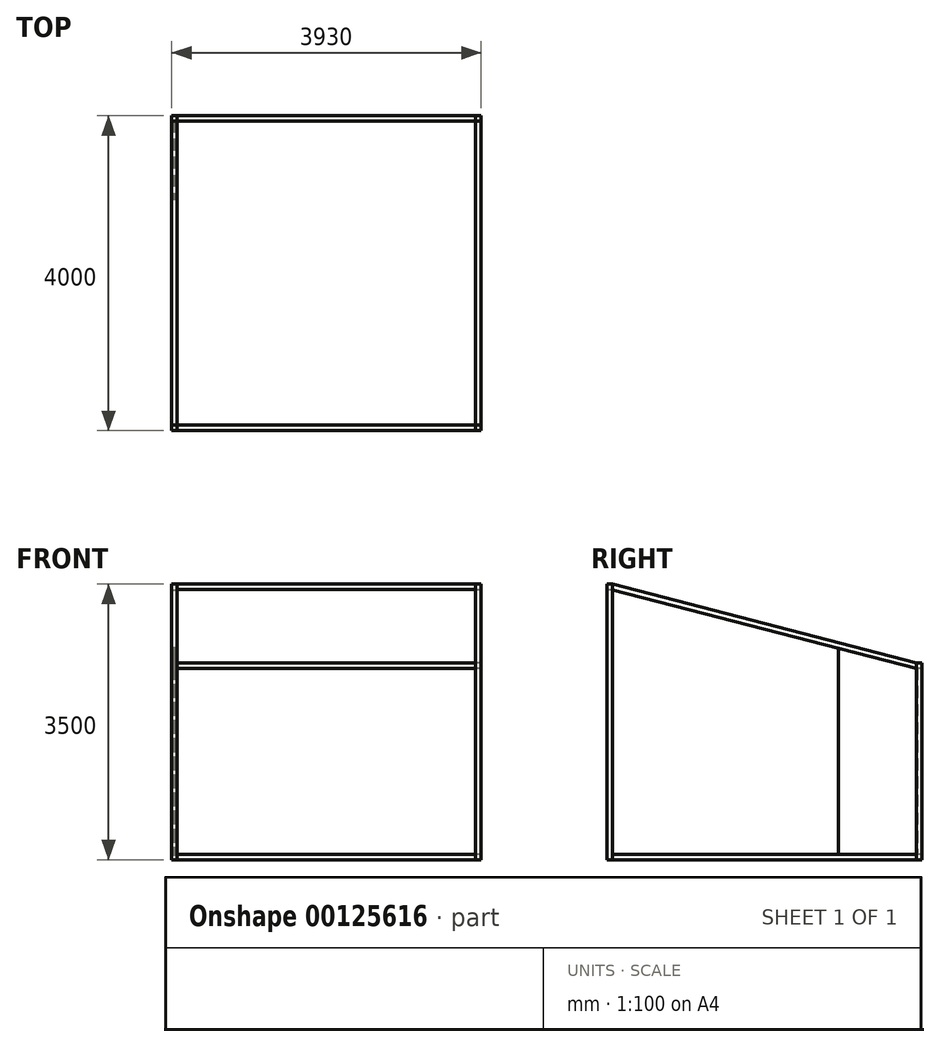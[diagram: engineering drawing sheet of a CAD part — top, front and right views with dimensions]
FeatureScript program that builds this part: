
annotation { "Feature Type Name" : "Feature", "Feature Type Description" : "" }
export const myFeature = defineFeature(function(context is Context, id is Id, definition is map)
    precondition{}
    {
        {
            assignVariable(context, id + "F0", {"name" : "D", "anyValue" : 70});
        }
        {
            var Q0;
            Q0=qCreatedBy(makeId("Front.planeOp"),FACE);
            var sketch = newSketch(context, id + "F1", { "sketchPlane" : qUnion([Q0])});
            skLineSegment(sketch, "E0.bottom", {"start": v(1965, -1750) * mm, "end": v(-1965, -1750) * mm});
            skLineSegment(sketch, "E0.top", {"start": v(1965, 1750) * mm, "end": v(-1965, 1750) * mm});
            skLineSegment(sketch, "E0.left", {"start": v(1965, -1750) * mm, "end": v(1965, 1750) * mm});
            skLineSegment(sketch, "E0.right", {"start": v(-1965, -1750) * mm, "end": v(-1965, 1750) * mm});
            skPoint(sketch, "E0.middle", {"position": v(0, 0) * mm});
            skSolve(sketch);
        }
        {
            var Q0;
            Q0=qCreatedBy(makeId("Front.planeOp"),FACE);
            var sketch = newSketch(context, id + "F2", { "sketchPlane" : qUnion([Q0])});
            skLineSegment(sketch, "E1.bottom", {"start": v(-1965, 1750) * mm, "end": v(-1895, 1750) * mm});
            skLineSegment(sketch, "E1.top", {"start": v(-1965, -1750) * mm, "end": v(-1895, -1750) * mm});
            skLineSegment(sketch, "E1.left", {"start": v(-1965, 1750) * mm, "end": v(-1965, -1750) * mm});
            skLineSegment(sketch, "E1.right", {"start": v(-1895, 1750) * mm, "end": v(-1895, -1750) * mm});
            skLineSegment(sketch, "E2", {"start": v(0, 1750) * mm, "end": v(0, -1750) * mm, "construction": true});
            skLineSegment(sketch, "E3.MirrorCS", {"start": v(1965, 1750) * mm, "end": v(1895, 1750) * mm});
            skLineSegment(sketch, "E4.MirrorCS", {"start": v(1965, -1750) * mm, "end": v(1895, -1750) * mm});
            skLineSegment(sketch, "E5.MirrorCS", {"start": v(1895, 1750) * mm, "end": v(1895, -1750) * mm});
            skLineSegment(sketch, "E6.MirrorCS", {"start": v(1965, 1750) * mm, "end": v(1965, -1750) * mm});
            skSolve(sketch);
        }
        {
            var Q0;
            Q0 = qSketchRegion(id + "F2", true);
            extrude(context, id + "F3", {"entities" : qUnion([Q0]), "depth" : (getVariable(context, 'D')) * mm});
        }
        {
            var Q0;
            Q0=makeQuery(id+"F1.imprint","IMPRINT",FACE,{"disambiguationData":[TD([[makeQuery(id+"F1.imprint","IMPRINT",EDGE,{"derivedFrom":sQuery(id+"F1.wireOp",EDGE,"E0.bottom")}),-1.0]])]});
            var sketch = newSketch(context, id + "F4", { "sketchPlane" : qUnion([Q0])});
            skLineSegment(sketch, "E7.bottom", {"start": v(-1895, 1750) * mm, "end": v(1895, 1750) * mm});
            skLineSegment(sketch, "E7.top", {"start": v(-1895, 1680) * mm, "end": v(1895, 1680) * mm});
            skLineSegment(sketch, "E7.left", {"start": v(-1895, 1750) * mm, "end": v(-1895, 1680) * mm});
            skLineSegment(sketch, "E7.right", {"start": v(1895, 1750) * mm, "end": v(1895, 1680) * mm});
            skSolve(sketch);
        }
        {
            var Q0;
            Q0 = qSketchRegion(id + "F4", true);
            extrude(context, id + "F5", {"entities" : qUnion([Q0]), "depth" : (getVariable(context, 'D')) * mm});
        }
        {
            var Q0;
            Q0=qCreatedBy(makeId("Right.planeOp"),FACE);
            var sketch = newSketch(context, id + "F6", { "sketchPlane" : qUnion([Q0])});
            skLineSegment(sketch, "E8", {"start": v(0, 1750) * mm, "end": v(3860, 750) * mm});
            skLineSegment(sketch, "E9", {"start": v(3860, 750) * mm, "end": v(3860, 677.69) * mm});
            skLineSegment(sketch, "E10", {"start": v(3860, 677.69) * mm, "end": v(0, 1677.69) * mm});
            skLineSegment(sketch, "E11", {"start": v(0, 1677.69) * mm, "end": v(0, 1750) * mm});
            skLineSegment(sketch, "E12.bottom", {"start": v(3860, -1750) * mm, "end": v(3930, -1750) * mm});
            skLineSegment(sketch, "E12.top", {"start": v(3860, 750) * mm, "end": v(3930, 750) * mm});
            skLineSegment(sketch, "E12.left", {"start": v(3860, -1750) * mm, "end": v(3860, 750) * mm});
            skLineSegment(sketch, "E12.right", {"start": v(3930, -1750) * mm, "end": v(3930, 750) * mm});
            skLineSegment(sketch, "E13.bottom", {"start": v(3860, -1750) * mm, "end": v(0, -1750) * mm});
            skLineSegment(sketch, "E13.top", {"start": v(3860, -1680) * mm, "end": v(0, -1680) * mm});
            skLineSegment(sketch, "E13.left", {"start": v(3860, -1750) * mm, "end": v(3860, -1680) * mm});
            skLineSegment(sketch, "E13.right", {"start": v(0, -1750) * mm, "end": v(0, -1680) * mm});
            skLineSegment(sketch, "E14", {"start": v(2860, 936.76) * mm, "end": v(2860, -1680) * mm});
            skSolve(sketch);
        }
        {
            var Q0;
            Q0=makeQuery(id+"F3.opExtrude","SWEPT_FACE",FACE,{"disambiguationData":[OSD([sQuery(id+"F2.wireOp",EDGE,"E1.left")])]});
            cPlane(context, id + "F7", {"entities" : qUnion([Q0]), "cplaneType" : CPlaneType.OFFSET, "offset" : (getVariable(context, 'D') / 2) * mm, "oppositeDirection" : true, "width" : 150 * mm, "height" : 150 * mm});
        }
        {
            var Q0;
            Q0=qCreatedBy(id+"F7.planeOp",FACE);
            var sketch = newSketch(context, id + "F8", { "sketchPlane" : qUnion([Q0])});
            skLineSegment(sketch, "E15.0", {"start": v(0, 1750) * mm, "end": v(-3860, 750) * mm});
            skLineSegment(sketch, "E15.1", {"start": v(0, 1677.69) * mm, "end": v(0, 1750) * mm});
            skLineSegment(sketch, "E15.2", {"start": v(-3860, 677.69) * mm, "end": v(0, 1677.69) * mm});
            skPoint(sketch, "E15.3", {"position": v(-3860, 677.69) * mm});
            skLineSegment(sketch, "E16", {"start": v(-3860, 750) * mm, "end": v(-3860, 677.69) * mm});
            skLineSegment(sketch, "E17.0", {"start": v(-3860, -1750) * mm, "end": v(-3860, -1680) * mm});
            skLineSegment(sketch, "E17.1", {"start": v(-3860, -1680) * mm, "end": v(0, -1680) * mm});
            skLineSegment(sketch, "E17.2", {"start": v(-3860, -1750) * mm, "end": v(0, -1750) * mm});
            skLineSegment(sketch, "E17.3", {"start": v(0, -1750) * mm, "end": v(0, -1680) * mm});
            skSolve(sketch);
        }
        {
            var Q0;
            Q0 = qSketchRegion(id + "F8", true);
            extrude(context, id + "F9", {"entities" : qUnion([Q0]), "depth" : (getVariable(context, 'D') / 2) * mm, "hasSecondDirection" : true, "secondDirectionOppositeDirection" : true, "secondDirectionDepth" : (getVariable(context, 'D') / 2) * mm});
        }
        {
            var Q0;
            Q0=makeQuery(id+"F9.opExtrude","SWEPT_BODY",BODY,{"disambiguationData":[OSD([sQuery(id+"F8.wireOp",EDGE,"E15.0"),sQuery(id+"F8.wireOp",EDGE,"E15.1"),sQuery(id+"F8.wireOp",EDGE,"E15.2"),sQuery(id+"F8.wireOp",EDGE,"E16")])]});
            var Q1;
            Q1=makeQuery(id+"F9.opExtrude","SWEPT_BODY",BODY,{"disambiguationData":[OSD([sQuery(id+"F8.wireOp",EDGE,"E17.0"),sQuery(id+"F8.wireOp",EDGE,"E17.1"),sQuery(id+"F8.wireOp",EDGE,"E17.2"),sQuery(id+"F8.wireOp",EDGE,"E17.3")])]});
            var Q2;
            Q2=qCreatedBy(makeId("Right.planeOp"),FACE);
            mirror(context, id + "F10", {"entities" : qUnion([Q0, Q1]), "mirrorPlane" : qUnion([Q2])});
        }
        {
            var Q0;
            Q0=makeQuery(id+"F9.opExtrude","SWEPT_FACE",FACE,{"disambiguationData":[OSD([sQuery(id+"F8.wireOp",EDGE,"E16")])]});
            var sketch = newSketch(context, id + "F11", { "sketchPlane" : qUnion([Q0])});
            skLineSegment(sketch, "E18.bottom", {"start": v(-1965, -1750) * mm, "end": v(-1895, -1750) * mm});
            skLineSegment(sketch, "E18.top", {"start": v(-1965, 750) * mm, "end": v(-1895, 750) * mm});
            skLineSegment(sketch, "E18.left", {"start": v(-1965, -1750) * mm, "end": v(-1965, 750) * mm});
            skLineSegment(sketch, "E18.right", {"start": v(-1895, -1750) * mm, "end": v(-1895, 750) * mm});
            skLineSegment(sketch, "E19.0", {"start": v(0, -1750) * mm, "end": v(0, 750) * mm, "construction": true});
            skLineSegment(sketch, "E20.MirrorCS", {"start": v(1965, 750) * mm, "end": v(1895, 750) * mm});
            skLineSegment(sketch, "E21.MirrorCS", {"start": v(1965, -1750) * mm, "end": v(1895, -1750) * mm});
            skLineSegment(sketch, "E22.MirrorCS", {"start": v(1965, -1750) * mm, "end": v(1965, 750) * mm});
            skLineSegment(sketch, "E23.MirrorCS", {"start": v(1895, -1750) * mm, "end": v(1895, 750) * mm});
            skLineSegment(sketch, "E24", {"start": v(0, -500) * mm, "end": v(1895, -500) * mm, "construction": true});
            skLineSegment(sketch, "E25.bottom", {"start": v(1895, 680) * mm, "end": v(-1895, 680) * mm});
            skLineSegment(sketch, "E25.top", {"start": v(1895, 750) * mm, "end": v(-1895, 750) * mm});
            skLineSegment(sketch, "E25.left", {"start": v(1895, 680) * mm, "end": v(1895, 750) * mm});
            skLineSegment(sketch, "E25.right", {"start": v(-1895, 680) * mm, "end": v(-1895, 750) * mm});
            skPoint(sketch, "E25.middle", {"position": v(0, 715) * mm});
            skLineSegment(sketch, "E26.MirrorCS", {"start": v(-1895, -1680) * mm, "end": v(-1895, -1750) * mm});
            skLineSegment(sketch, "E27.MirrorCS", {"start": v(1895, -1680) * mm, "end": v(1895, -1750) * mm});
            skPoint(sketch, "E28.MirrorP", {"position": v(0, -1715) * mm});
            skLineSegment(sketch, "E29.MirrorCS", {"start": v(1895, -1680) * mm, "end": v(-1895, -1680) * mm});
            skLineSegment(sketch, "E30.MirrorCS", {"start": v(1895, -1750) * mm, "end": v(-1895, -1750) * mm});
            skSolve(sketch);
        }
        {
            var Q0;
            Q0 = qSketchRegion(id + "F11", true);
            extrude(context, id + "F12", {"entities" : qUnion([Q0]), "depth" : (getVariable(context, 'D')) * mm});
        }
        {
            var Q0;
            Q0=qCreatedBy(id+"F7.planeOp",FACE);
            var sketch = newSketch(context, id + "F13", { "sketchPlane" : qUnion([Q0])});
            skLineSegment(sketch, "E31.bottom", {"start": v(-3870, 685.43) * mm, "end": v(-2870, 944.5) * mm});
            skLineSegment(sketch, "E31.top", {"start": v(-3870, -1690) * mm, "end": v(-2870, -1690) * mm});
            skLineSegment(sketch, "E31.left", {"start": v(-3870, 685.43) * mm, "end": v(-3870, -1690) * mm});
            skLineSegment(sketch, "E31.right", {"start": v(-2870, 944.5) * mm, "end": v(-2870, -1690) * mm});
            skSolve(sketch);
        }
        {
            var Q0;
            Q0 = qSketchRegion(id + "F13", true);
            extrude(context, id + "F14", {"entities" : qUnion([Q0]), "endBound" : BoundingType.SYMMETRIC, "depth" : 18 * mm});
        }
    });
